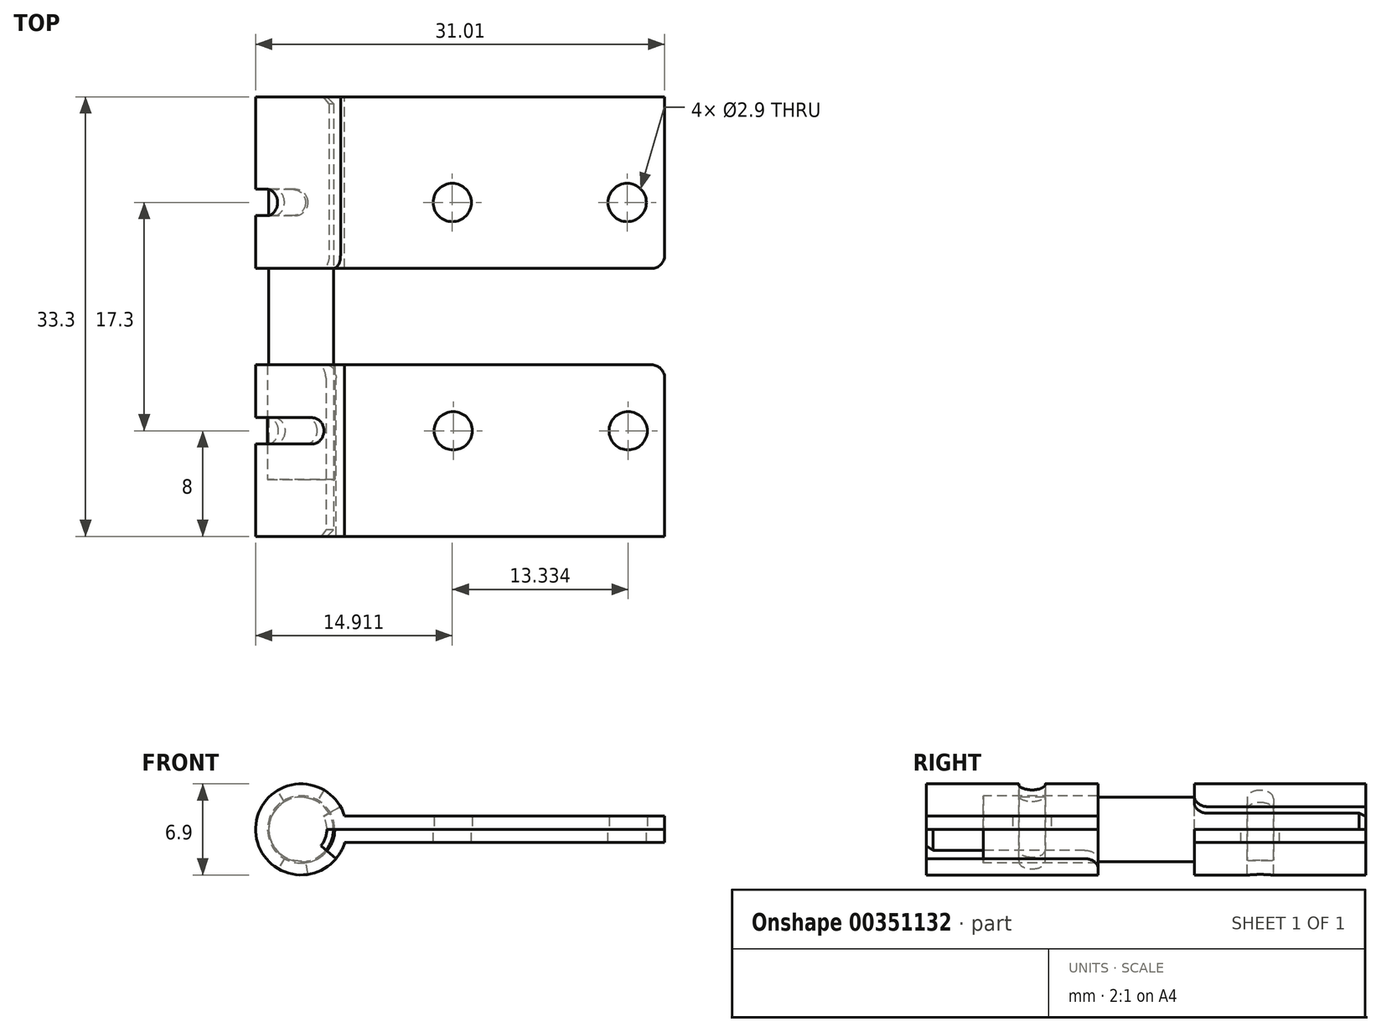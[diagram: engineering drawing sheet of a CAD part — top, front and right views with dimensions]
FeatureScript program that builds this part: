
annotation { "Feature Type Name" : "Feature", "Feature Type Description" : "" }
export const myFeature = defineFeature(function(context is Context, id is Id, definition is map)
    precondition{}
    {
        {
            var Q0;
            Q0=qCreatedBy(makeId("Top.planeOp"),FACE);
            var sketch = newSketch(context, id + "F0", { "sketchPlane" : qUnion([Q0])});
            skLineSegment(sketch, "E0.bottom", {"start": v(1.22, 13.65) * mm, "end": v(-1.23, 13.65) * mm});
            skLineSegment(sketch, "E0.top", {"start": v(1.23, -13.65) * mm, "end": v(-1.23, -13.65) * mm});
            skLineSegment(sketch, "E0.left", {"start": v(1.22, 13.65) * mm, "end": v(1.23, -13.65) * mm});
            skLineSegment(sketch, "E0.right", {"start": v(-1.23, 13.65) * mm, "end": v(-1.23, -13.65) * mm});
            skPoint(sketch, "E0.middle", {"position": v(0, 0) * mm});
            skLineSegment(sketch, "E1", {"start": v(-1.23, -13.65) * mm, "end": v(-2.23, -13.65) * mm});
            skLineSegment(sketch, "E2", {"start": v(-2.23, -13.65) * mm, "end": v(-2.23, -3.65) * mm});
            skLineSegment(sketch, "E3", {"start": v(-2.23, -3.65) * mm, "end": v(-1.23, -3.65) * mm});
            skLineSegment(sketch, "E4.MirrorCS", {"start": v(1.22, 13.65) * mm, "end": v(3.67, 13.65) * mm});
            skLineSegment(sketch, "E5.MirrorCS", {"start": v(3.67, 13.65) * mm, "end": v(3.68, -13.65) * mm});
            skLineSegment(sketch, "E6.MirrorCS", {"start": v(1.23, -13.65) * mm, "end": v(3.68, -13.65) * mm});
            skLineSegment(sketch, "E7", {"start": v(3.67, 13.65) * mm, "end": v(4.67, 13.65) * mm});
            skLineSegment(sketch, "E8", {"start": v(4.67, 13.65) * mm, "end": v(4.67, 3.65) * mm});
            skLineSegment(sketch, "E9", {"start": v(4.67, 3.65) * mm, "end": v(3.67, 3.65) * mm});
            skSolve(sketch);
        }
        {
            var Q0;
            Q0=makeQuery(id+"F0.imprint","IMPRINT",FACE,{"disambiguationData":[TD([[makeQuery(id+"F0.imprint","IMPRINT",EDGE,{"derivedFrom":sQuery(id+"F0.wireOp",EDGE,"E0.bottom")}),1.0]])]});
            var Q1;
            Q1=sQuery(id+"F0.wireOp",EDGE,"E0.left");
            revolve(context, id + "F1", {"entities" : qUnion([Q0]), "axis" : qUnion([Q1]), "revolveType" : RevolveType.FULL});
        }
        {
            var Q0;
            {var subQ0=sQuery(id+"F0.wireOp",EDGE,"E1");Q0=makeQuery(id+"F0.imprint","IMPRINT",FACE,{"disambiguationData":[TD([[makeQuery(id+"F0.imprint","IMPRINT",EDGE,{"derivedFrom":subQ0}),-1.0]])]});}
            var Q1;
            Q1=sQuery(id+"F0.wireOp",EDGE,"E0.left");
            revolve(context, id + "F2", {"entities" : qUnion([Q0]), "axis" : qUnion([Q1]), "revolveType" : RevolveType.TWO_DIRECTIONS, "angle" : 140 * degree, "angleBack" : 180 * degree});
        }
        {
            var Q0;
            {var subQ0=sQuery(id+"F0.wireOp",EDGE,"E7");Q0=makeQuery(id+"F0.imprint","IMPRINT",FACE,{"disambiguationData":[TD([[makeQuery(id+"F0.imprint","IMPRINT",EDGE,{"derivedFrom":subQ0}),-1.0]])]});}
            var Q1;
            Q1=sQuery(id+"F0.wireOp",EDGE,"E0.left");
            revolve(context, id + "F3", {"entities" : qUnion([Q0]), "axis" : qUnion([Q1]), "revolveType" : RevolveType.TWO_DIRECTIONS, "angle" : 0 * degree, "angleBack" : 30 * degree});
        }
        {
            var Q0;
            Q0=makeQuery(id+"F2.opRevolve","CAP_FACE",FACE,{"disambiguationData":[OSD([sQuery(id+"F0.wireOp",EDGE,"E0.right"),sQuery(id+"F0.wireOp",EDGE,"E1"),sQuery(id+"F0.wireOp",EDGE,"E2"),sQuery(id+"F0.wireOp",EDGE,"E3")])],"isStart":true});
            var sketch = newSketch(context, id + "F4", { "sketchPlane" : qUnion([Q0])});
            skLineSegment(sketch, "E10.bottom", {"start": v(3.68, 13.65) * mm, "end": v(28.77, 13.65) * mm});
            skLineSegment(sketch, "E10.top", {"start": v(3.67, 3.65) * mm, "end": v(28.77, 3.65) * mm});
            skLineSegment(sketch, "E10.left", {"start": v(3.68, 13.65) * mm, "end": v(3.68, 3.65) * mm});
            skLineSegment(sketch, "E10.right", {"start": v(28.77, 13.65) * mm, "end": v(28.77, 3.65) * mm});
            skLineSegment(sketch, "E11", {"start": v(-2.23, 3.65) * mm, "end": v(-2.23, 13.65) * mm});
            skLineSegment(sketch, "E12", {"start": v(-2.23, 8.65) * mm, "end": v(28.77, 8.65) * mm, "construction": true});
            skCircle(sketch, "E13", {"center": v(12.76, 8.65) * mm, "radius": 1.45 * mm});
            skCircle(sketch, "E14", {"center": v(26.02, 8.65) * mm, "radius": 1.45 * mm});
            skLineSegment(sketch, "E15.0", {"start": v(4.67, 3.65) * mm, "end": v(-2.23, 3.65) * mm});
            skLineSegment(sketch, "E16.0", {"start": v(4.68, 13.65) * mm, "end": v(-2.23, 13.65) * mm});
            skLineSegment(sketch, "E17", {"start": v(1.22, 3.65) * mm, "end": v(1.23, 13.65) * mm, "construction": true});
            skLineSegment(sketch, "E18.bottom", {"start": v(-3.23, 7.65) * mm, "end": v(-1.23, 7.65) * mm});
            skLineSegment(sketch, "E18.top", {"start": v(-3.23, 9.65) * mm, "end": v(-1.23, 9.65) * mm});
            skLineSegment(sketch, "E18.left", {"start": v(-3.23, 7.65) * mm, "end": v(-3.23, 9.65) * mm});
            skLineSegment(sketch, "E18.right", {"start": v(-1.23, 7.65) * mm, "end": v(-1.23, 9.65) * mm});
            skPoint(sketch, "E18.middle", {"position": v(-2.23, 8.65) * mm});
            skLineSegment(sketch, "E19", {"start": v(1.22, 3.65) * mm, "end": v(-1.32, 3.65) * mm});
            skLineSegment(sketch, "E20", {"start": v(-1.32, 3.65) * mm, "end": v(-1.32, 12.35) * mm});
            skLineSegment(sketch, "E21", {"start": v(-1.32, 12.35) * mm, "end": v(1.23, 12.35) * mm});
            skLineSegment(sketch, "E22", {"start": v(1.23, 12.35) * mm, "end": v(1.22, 3.65) * mm});
            skSolve(sketch);
        }
        {
            var Q0;
            {var subQ2=sQuery(id+"F4.wireOp",EDGE,"E10.right");Q0=makeQuery(id+"F4.imprint","IMPRINT",FACE,{"disambiguationData":[TD([[makeQuery(id+"F4.imprint","IMPRINT",EDGE,{"derivedFrom":subQ2}),-1.0]])]});}
            var Q1;
            {var subQ0=sQuery(id+"F4.wireOp",EDGE,"E10.left");Q1=makeQuery(id+"F4.imprint","IMPRINT",FACE,{"disambiguationData":[TD([[makeQuery(id+"F4.imprint","IMPRINT",EDGE,{"derivedFrom":subQ0}),-1.0]])]});}
            var Q2;
            {var subQ0=sQuery(id+"F4.wireOp",EDGE,"b2c81ba9-bbb6-4e08-98fd-638bb6d25fa10.MirrorCS");Q2=makeQuery(id+"F4.imprint","IMPRINT",FACE,{"disambiguationData":[TD([[makeQuery(id+"F4.imprint","IMPRINT",EDGE,{"derivedFrom":subQ0}),-1.0]])]});}
            extrude(context, id + "F5", {"entities" : qUnion([Q0, Q1, Q2]), "operationType" : NewBodyOperationType.ADD, "oppositeDirection" : true, "depth" : 1 * mm});
        }
        {
            var Q0;
            Q0=makeQuery(id+"F3.opRevolve","CAP_FACE",FACE,{"disambiguationData":[OSD([sQuery(id+"F0.wireOp",EDGE,"E5.MirrorCS"),sQuery(id+"F0.wireOp",EDGE,"E7"),sQuery(id+"F0.wireOp",EDGE,"E8"),sQuery(id+"F0.wireOp",EDGE,"E9")])],"isStart":false});
            var sketch = newSketch(context, id + "F6", { "sketchPlane" : qUnion([Q0])});
            skPoint(sketch, "E23.oppositeSnap0", {"position": v(4.17, 3.65) * mm});
            skLineSegment(sketch, "E23.bottom", {"start": v(3.67, 13.65) * mm, "end": v(28.77, 13.65) * mm});
            skLineSegment(sketch, "E23.top", {"start": v(3.67, 3.65) * mm, "end": v(28.77, 3.65) * mm});
            skLineSegment(sketch, "E23.left", {"start": v(3.67, 13.65) * mm, "end": v(3.67, 3.65) * mm});
            skLineSegment(sketch, "E23.right", {"start": v(28.77, 13.65) * mm, "end": v(28.77, 3.65) * mm});
            skSolve(sketch);
        }
        {
            var Q0;
            Q0 = qSketchRegion(id + "F6", true);
            extrude(context, id + "F7", {"entities" : qUnion([Q0]), "operationType" : NewBodyOperationType.ADD, "oppositeDirection" : true, "depth" : 1 * mm});
        }
        {
            var Q0;
            Q0=makeQuery(id+"F1.opRevolve","SWEPT_FACE",FACE,{"disambiguationData":[OSD([sQuery(id+"F0.wireOp",EDGE,"E0.bottom")])]});
            extrude(context, id + "F8", {"entities" : qUnion([Q0]), "operationType" : NewBodyOperationType.ADD, "depth" : 3 * mm});
        }
        {
            var Q0;
            Q0=makeQuery(id+"F1.opRevolve","SWEPT_FACE",FACE,{"disambiguationData":[OSD([sQuery(id+"F0.wireOp",EDGE,"E0.top")])]});
            extrude(context, id + "F9", {"entities" : qUnion([Q0]), "operationType" : NewBodyOperationType.ADD, "depth" : 3 * mm});
        }
        {
            var Q0;
            Q0=makeQuery(id+"F8.opExtrude","CAP_EDGE",EDGE,{"disambiguationData":[OSD([sQuery(id+"F0.wireOp",EDGE,"E0.bottom"),sQuery(id+"F0.wireOp",EDGE,"E0.right")])],"isStart":false});
            var Q1;
            Q1=makeQuery(id+"F9.opExtrude","CAP_EDGE",EDGE,{"disambiguationData":[OSD([sQuery(id+"F0.wireOp",EDGE,"E0.top"),sQuery(id+"F0.wireOp",EDGE,"E0.right"),sQuery(id+"F0.wireOp",EDGE,"E1")])],"isStart":false});
            chamfer(context, id + "F10", {"entities" : qUnion([Q0, Q1]), "width" : 0.5 * mm, "tangentPropagation" : true});
        }
        {
            var Q0;
            Q0=makeQuery(id+"F7.boolean.opBoolean","MERGE",FACE,{"derivedFrom":[makeQuery(id+"F3.opRevolve","CAP_FACE",FACE,{"disambiguationData":[OSD([sQuery(id+"F0.wireOp",EDGE,"E5.MirrorCS"),sQuery(id+"F0.wireOp",EDGE,"E7"),sQuery(id+"F0.wireOp",EDGE,"E8"),sQuery(id+"F0.wireOp",EDGE,"E9")])],"isStart":false}),makeQuery(id+"F7.opExtrude","CAP_FACE",FACE,{"disambiguationData":[OSD([sQuery(id+"F6.wireOp",EDGE,"E23.bottom"),sQuery(id+"F6.wireOp",EDGE,"E23.top"),sQuery(id+"F6.wireOp",EDGE,"E23.left"),sQuery(id+"F6.wireOp",EDGE,"E23.right")])],"isStart":true})]});
            var sketch = newSketch(context, id + "F11", { "sketchPlane" : qUnion([Q0])});
            skLineSegment(sketch, "E24.0", {"start": v(28.77, 3.65) * mm, "end": v(3.67, 3.65) * mm});
            skLineSegment(sketch, "E25.0", {"start": v(3.67, 13.65) * mm, "end": v(28.77, 13.65) * mm});
            skLineSegment(sketch, "E26.0", {"start": v(28.77, 13.65) * mm, "end": v(28.77, 3.65) * mm});
            skLineSegment(sketch, "E27", {"start": v(-2.23, 3.65) * mm, "end": v(-2.23, 13.65) * mm});
            skLineSegment(sketch, "E28.0", {"start": v(4.53, 3.65) * mm, "end": v(-2.23, 3.65) * mm});
            skLineSegment(sketch, "E29.0", {"start": v(4.53, 13.65) * mm, "end": v(-2.23, 13.65) * mm});
            skLineSegment(sketch, "E30", {"start": v(1.15, 13.65) * mm, "end": v(1.15, 3.65) * mm, "construction": true});
            skCircle(sketch, "E31", {"center": v(12.68, 8.65) * mm, "radius": 1.45 * mm});
            skCircle(sketch, "E32", {"center": v(25.94, 8.65) * mm, "radius": 1.45 * mm});
            skLineSegment(sketch, "E33", {"start": v(-2.23, 8.65) * mm, "end": v(28.77, 8.65) * mm, "construction": true});
            skLineSegment(sketch, "E34.bottom", {"start": v(-3.23, 9.65) * mm, "end": v(-1.23, 9.65) * mm});
            skLineSegment(sketch, "E34.top", {"start": v(-3.23, 7.65) * mm, "end": v(-1.23, 7.65) * mm});
            skLineSegment(sketch, "E34.left", {"start": v(-3.23, 9.65) * mm, "end": v(-3.23, 7.65) * mm});
            skLineSegment(sketch, "E34.right", {"start": v(-1.23, 9.65) * mm, "end": v(-1.23, 7.65) * mm});
            skPoint(sketch, "E34.middle", {"position": v(-2.23, 8.65) * mm});
            skSolve(sketch);
        }
        {
            var Q0;
            Q0=makeQuery(id+"F11.imprint","IMPRINT",FACE,{"disambiguationData":[TD([[makeQuery(id+"F11.imprint","IMPRINT",EDGE,{"derivedFrom":sQuery(id+"F11.wireOp",EDGE,"E31")}),1.0]])]});
            var Q1;
            Q1=makeQuery(id+"F11.imprint","IMPRINT",FACE,{"disambiguationData":[TD([[makeQuery(id+"F11.imprint","IMPRINT",EDGE,{"derivedFrom":sQuery(id+"F11.wireOp",EDGE,"E32")}),1.0]])]});
            extrude(context, id + "F12", {"entities" : qUnion([Q0, Q1]), "operationType" : NewBodyOperationType.REMOVE, "endBound" : BoundingType.UP_TO_NEXT, "oppositeDirection" : true, "depth" : 25 * mm});
        }
        {
            var Q0;
            {var subQ5=sQuery(id+"F11.wireOp",EDGE,"E34.left");Q0=makeQuery(id+"F11.imprint","IMPRINT",FACE,{"disambiguationData":[TD([[makeQuery(id+"F11.imprint","IMPRINT",EDGE,{"derivedFrom":subQ5}),1.0]])]});}
            var Q1;
            {var subQ5=sQuery(id+"F11.wireOp",EDGE,"E34.right");Q1=makeQuery(id+"F11.imprint","IMPRINT",FACE,{"disambiguationData":[TD([[makeQuery(id+"F11.imprint","IMPRINT",EDGE,{"derivedFrom":subQ5}),-1.0]])]});}
            var Q2;
            Q2=sQuery(id+"F11.wireOp",EDGE,"E30");
            revolve(context, id + "F13", {"operationType" : NewBodyOperationType.REMOVE, "entities" : qUnion([Q0, Q1]), "axis" : qUnion([Q2]), "revolveType" : RevolveType.TWO_DIRECTIONS, "oppositeDirection" : true, "angle" : 60 * degree, "angleBack" : 260 * degree});
        }
        {
            var Q0;
            Q0=makeQuery(id+"F13.boolean.opBoolean","COPY",EDGE,{"derivedFrom":makeQuery(id+"F13.opRevolve","CAP_EDGE",EDGE,{"disambiguationData":[OSD([sQuery(id+"F11.wireOp",EDGE,"E34.bottom")])],"isStart":false})});
            var Q1;
            Q1=makeQuery(id+"F13.boolean.opBoolean","COPY",EDGE,{"derivedFrom":makeQuery(id+"F13.opRevolve","CAP_EDGE",EDGE,{"disambiguationData":[OSD([sQuery(id+"F11.wireOp",EDGE,"E34.top")])],"isStart":false})});
            var Q2;
            Q2=makeQuery(id+"F13.boolean.opBoolean","COPY",EDGE,{"derivedFrom":makeQuery(id+"F13.opRevolve","CAP_EDGE",EDGE,{"disambiguationData":[OSD([sQuery(id+"F11.wireOp",EDGE,"E34.bottom")])],"isStart":true})});
            var Q3;
            Q3=makeQuery(id+"F13.boolean.opBoolean","COPY",EDGE,{"derivedFrom":makeQuery(id+"F13.opRevolve","CAP_EDGE",EDGE,{"disambiguationData":[OSD([sQuery(id+"F11.wireOp",EDGE,"E34.top")])],"isStart":true})});
            fillet(context, id + "F14", {"entities" : qUnion([Q0, Q1, Q2, Q3]), "radius" : 1 * mm, "tangentPropagation" : true, "allowEdgeOverflow" : false});
        }
        {
            var Q0;
            {var subQ5=sQuery(id+"F4.wireOp",EDGE,"E18.left");Q0=makeQuery(id+"F4.imprint","IMPRINT",FACE,{"disambiguationData":[TD([[makeQuery(id+"F4.imprint","IMPRINT",EDGE,{"derivedFrom":subQ5}),-1.0]])]});}
            var Q1;
            {var subQ5=sQuery(id+"F4.wireOp",EDGE,"E18.right");Q1=makeQuery(id+"F4.imprint","IMPRINT",FACE,{"disambiguationData":[TD([[makeQuery(id+"F4.imprint","IMPRINT",EDGE,{"derivedFrom":subQ5}),1.0]])]});}
            var Q2;
            {var subQ0=sQuery(id+"F4.wireOp",EDGE,"E18.bottom");var subQ1=sQuery(id+"F4.wireOp",EDGE,"E11");var subQ2=makeQuery(id+"F4.imprint","INTERSECT",VERTEX,{"derivedFrom":[subQ1,subQ0]});Q2=makeQuery(id+"F4.imprint","IMPRINT",FACE,{"disambiguationData":[TD([[makeQuery(id+"F4.imprint","IMPRINT",EDGE,{"disambiguationData":[TD([[subQ2,-1.0]])],"derivedFrom":subQ1}),-1.0]])]});}
            var Q3;
            Q3=sQuery(id+"F4.wireOp",EDGE,"E17");
            revolve(context, id + "F15", {"operationType" : NewBodyOperationType.REMOVE, "entities" : qUnion([Q0, Q1, Q2]), "axis" : qUnion([Q3]), "revolveType" : RevolveType.TWO_DIRECTIONS, "oppositeDirection" : true, "angle" : 120 * degree, "angleBack" : 300 * degree});
        }
        {
            var Q0;
            Q0=makeQuery(id+"F15.boolean.opBoolean","COPY",EDGE,{"derivedFrom":makeQuery(id+"F15.opRevolve","CAP_EDGE",EDGE,{"disambiguationData":[OSD([sQuery(id+"F4.wireOp",EDGE,"E18.bottom")])],"isStart":false})});
            var Q1;
            Q1=makeQuery(id+"F15.boolean.opBoolean","COPY",EDGE,{"derivedFrom":makeQuery(id+"F15.opRevolve","CAP_EDGE",EDGE,{"disambiguationData":[OSD([sQuery(id+"F4.wireOp",EDGE,"E18.bottom")])],"isStart":true})});
            var Q2;
            Q2=makeQuery(id+"F15.boolean.opBoolean","COPY",EDGE,{"derivedFrom":makeQuery(id+"F15.opRevolve","CAP_EDGE",EDGE,{"disambiguationData":[OSD([sQuery(id+"F4.wireOp",EDGE,"E18.top")])],"isStart":true})});
            var Q3;
            Q3=makeQuery(id+"F15.boolean.opBoolean","COPY",EDGE,{"derivedFrom":makeQuery(id+"F15.opRevolve","CAP_EDGE",EDGE,{"disambiguationData":[OSD([sQuery(id+"F4.wireOp",EDGE,"E18.top")])],"isStart":false})});
            fillet(context, id + "F16", {"entities" : qUnion([Q0, Q1, Q2, Q3]), "radius" : 1 * mm, "tangentPropagation" : true, "allowEdgeOverflow" : false});
        }
        {
            var Q0;
            Q0=makeQuery(id+"F5.opExtrude","SWEPT_EDGE",EDGE,{"disambiguationData":[OSD([sQuery(id+"F4.wireOp",EDGE,"E10.bottom"),sQuery(id+"F4.wireOp",EDGE,"E10.right")])]});
            var Q1;
            Q1=makeQuery(id+"F5.opExtrude","SWEPT_EDGE",EDGE,{"disambiguationData":[OSD([sQuery(id+"F4.wireOp",EDGE,"E10.top"),sQuery(id+"F4.wireOp",EDGE,"E10.right")])]});
            var Q2;
            Q2=makeQuery(id+"F7.opExtrude","SWEPT_EDGE",EDGE,{"disambiguationData":[OSD([sQuery(id+"F6.wireOp",EDGE,"E23.top"),sQuery(id+"F6.wireOp",EDGE,"E23.right")])]});
            var Q3;
            Q3=makeQuery(id+"F7.opExtrude","SWEPT_EDGE",EDGE,{"disambiguationData":[OSD([sQuery(id+"F6.wireOp",EDGE,"E23.bottom"),sQuery(id+"F6.wireOp",EDGE,"E23.right")])]});
            var Q4;
            Q4=makeQuery(id+"F2.opRevolve","CAP_EDGE",EDGE,{"disambiguationData":[OSD([sQuery(id+"F0.wireOp",EDGE,"E1")])],"isStart":false});
            var Q5;
            Q5=makeQuery(id+"F2.opRevolve","CAP_EDGE",EDGE,{"disambiguationData":[OSD([sQuery(id+"F0.wireOp",EDGE,"E3")])],"isStart":false});
            var Q6;
            Q6=makeQuery(id+"F3.opRevolve","CAP_EDGE",EDGE,{"disambiguationData":[OSD([sQuery(id+"F0.wireOp",EDGE,"E9")])],"isStart":true});
            var Q7;
            Q7=makeQuery(id+"F3.opRevolve","CAP_EDGE",EDGE,{"disambiguationData":[OSD([sQuery(id+"F0.wireOp",EDGE,"E7")])],"isStart":true});
            fillet(context, id + "F17", {"entities" : qUnion([Q0, Q1, Q2, Q3, Q4, Q5, Q6, Q7]), "radius" : 1 * mm, "tangentPropagation" : true, "allowEdgeOverflow" : false});
        }
        {
            var Q0;
            {var subQ1=sQuery(id+"F4.wireOp",EDGE,"E18.right");Q0=makeQuery(id+"F4.imprint","IMPRINT",FACE,{"disambiguationData":[TD([[makeQuery(id+"F4.imprint","IMPRINT",EDGE,{"derivedFrom":subQ1}),-1.0]])]});}
            var Q1;
            {var subQ0=sQuery(id+"F4.wireOp",EDGE,"E18.right");Q1=makeQuery(id+"F4.imprint","IMPRINT",FACE,{"disambiguationData":[TD([[makeQuery(id+"F4.imprint","IMPRINT",EDGE,{"derivedFrom":subQ0}),1.0]])]});}
            var Q2;
            Q2=sQuery(id+"F4.wireOp",EDGE,"E22");
            revolve(context, id + "F18", {"entities" : qUnion([Q0, Q1]), "axis" : qUnion([Q2]), "revolveType" : RevolveType.FULL});
        }
    });
